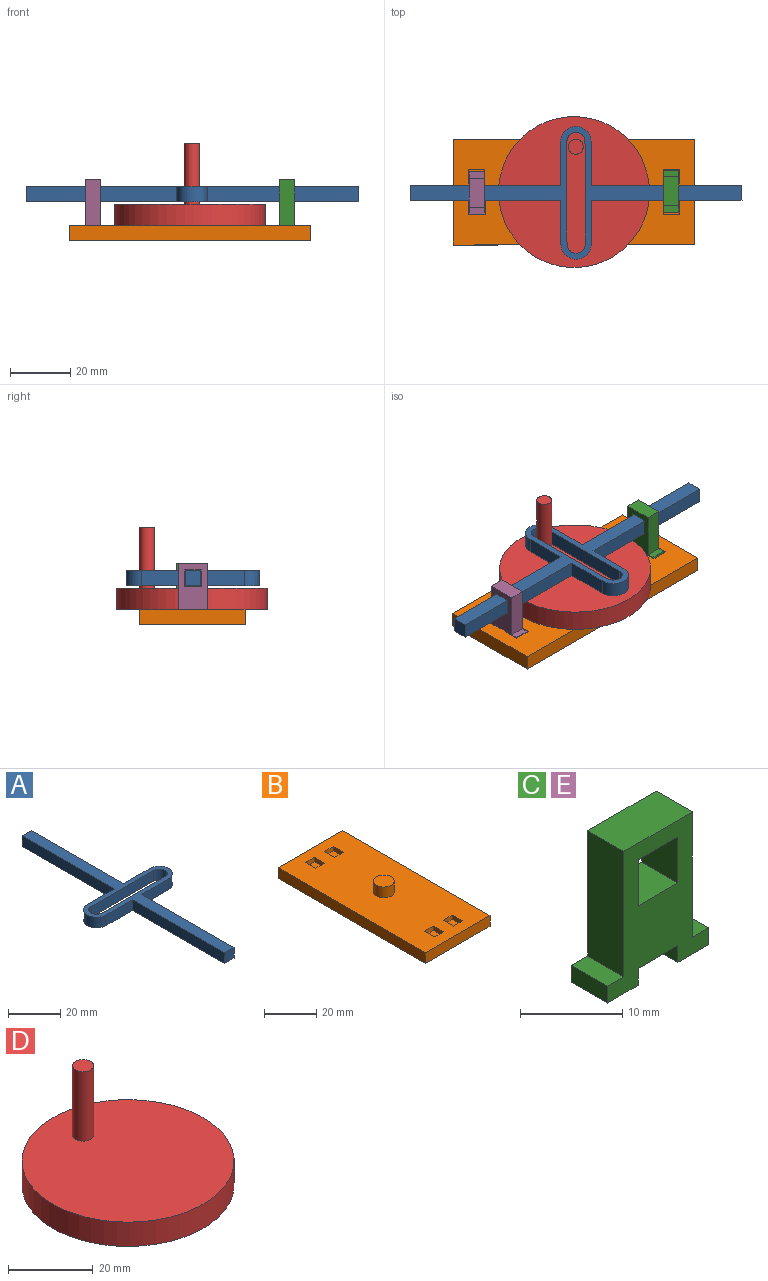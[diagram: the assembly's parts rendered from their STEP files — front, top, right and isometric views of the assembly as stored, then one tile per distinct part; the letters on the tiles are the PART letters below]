
ASSEMBLY  parts=5 mates=4
PART A: 18 faces, bbox 44x110x5 mm
  f0: extruded ~6x5mm, area 47.1mm2, adj f1,f15,f16,f17
  f1: plane 34x5mm, normal (0,-1,0), area 170mm2, adj f0,f2,f16,f17
  f2: cylinder r=3mm len=6mm, axis (0,0,-1), area 47.1mm2, adj f1,f15,f16,f17
  f3: plane 50x5mm, normal (-1,0,0), area 250mm2, adj f4,f14,f16,f17
  f4: plane 14.5x5mm, normal (0,1,0), area 72.5mm2, adj f3,f5,f16,f17
  f5: cylinder r=5mm len=10mm, axis (0,0,-1), area 78.5mm2, adj f4,f6,f16,f17
  f6: plane 14.5x5mm, normal (0,-1,0), area 72.5mm2, adj f5,f7,f16,f17
  f7: plane 50x5mm, normal (-1,0,0), area 250mm2, adj f6,f8,f16,f17
  f8: plane 5x5mm, normal (0,-1,0), area 25mm2, adj f7,f9,f16,f17
  f9: plane 50x5mm, normal (1,0,0), area 250mm2, adj f8,f10,f16,f17
  f10: plane 14.5x5mm, normal (0,-1,0), area 72.5mm2, adj f9,f11,f16,f17
  f11: cylinder r=5mm len=10mm, axis (0,0,-1), area 78.5mm2, adj f10,f12,f16,f17
  f12: plane 14.5x5mm, normal (0,1,0), area 72.5mm2, adj f11,f13,f16,f17
  f13: plane 50x5mm, normal (1,0,0), area 250mm2, adj f12,f14,f16,f17
  f14: plane 5x5mm, normal (0,1,0), area 25mm2, adj f3,f13,f16,f17
  f15: plane 34x5mm, normal (0,1,0), area 170mm2, adj f0,f2,f16,f17
  f16: plane 110x44mm, normal (0,0,1), area 686.3mm2, adj f0,f1,f2,f3,f4,f5,f6,f7
  f17: plane 110x44mm, normal (0,0,-1), area 686.3mm2, adj f0,f1,f2,f3,f4,f5,f6,f7
PART B: 28 faces, bbox 35x80x10 mm
  f0: plane 80x35mm, normal (0,0,1), area 2645.2mm2, adj f1,f2,f3,f4,f6,f7,f8,f9
  f1: plane 80x5mm, normal (1,0,0), area 400mm2, adj f0,f2,f4,f5
  f2: plane 35x5mm, normal (0,1,0), area 175mm2, adj f0,f1,f3,f5
  f3: plane 80x5mm, normal (-1,0,0), area 400mm2, adj f0,f2,f4,f5
  f4: plane 35x5mm, normal (0,-1,0), area 175mm2, adj f0,f1,f3,f5
  f5: plane 80x35mm, normal (0,0,-1), area 2800mm2, adj f1,f2,f3,f4
  f6: plane 5.5x2mm, normal (-1,0,0), area 11mm2, adj f0,f7,f9,f10
  f7: plane 4.75x2mm, normal (0,-1,0), area 9.5mm2, adj f0,f6,f8,f10
  f8: plane 5.5x2mm, normal (1,0,0), area 11mm2, adj f0,f7,f9,f10
  f9: plane 4.75x2mm, normal (0,1,0), area 9.5mm2, adj f0,f6,f8,f10
  f10: plane 5.5x4.75mm, normal (0,0,1), area 26.1mm2, adj f6,f7,f8,f9
  f11: plane 4.75x2mm, normal (0,-1,0), area 9.5mm2, adj f0,f12,f14,f15
  f12: plane 5.5x2mm, normal (1,0,0), area 11mm2, adj f0,f11,f13,f15
  f13: plane 4.75x2mm, normal (0,1,0), area 9.5mm2, adj f0,f12,f14,f15
  f14: plane 5.5x2mm, normal (-1,0,0), area 11mm2, adj f0,f11,f13,f15
  f15: plane 5.5x4.75mm, normal (0,0,1), area 26.1mm2, adj f11,f12,f13,f14
  f16: plane 4.75x2mm, normal (0,1,0), area 9.5mm2, adj f0,f17,f19,f20
  f17: plane 5.5x2mm, normal (-1,0,0), area 11mm2, adj f0,f16,f18,f20
  f18: plane 4.75x2mm, normal (0,-1,0), area 9.5mm2, adj f0,f17,f19,f20
  f19: plane 5.5x2mm, normal (1,0,0), area 11mm2, adj f0,f16,f18,f20
  f20: plane 5.5x4.75mm, normal (0,0,1), area 26.1mm2, adj f16,f17,f18,f19
  f21: plane 5.5x2mm, normal (-1,0,0), area 11mm2, adj f0,f22,f24,f25
  f22: plane 4.75x2mm, normal (0,-1,0), area 9.5mm2, adj f0,f21,f23,f25
  f23: plane 5.5x2mm, normal (1,0,0), area 11mm2, adj f0,f22,f24,f25
  f24: plane 4.75x2mm, normal (0,1,0), area 9.5mm2, adj f0,f21,f23,f25
  f25: plane 5.5x4.75mm, normal (0,0,1), area 26.1mm2, adj f21,f22,f23,f24
  f26: cylinder r=4mm len=8mm, axis (0,0,-1), area 125.7mm2, adj f0,f27
  f27: plane 8x8mm, normal (0,0,1), area 50.3mm2, adj f26
PART C: 18 faces, bbox 14x5x17 mm
  f0: plane 17x14mm, normal (0,1,0), area 129.2mm2, adj f2,f3,f4,f5,f6,f7,f8,f9
  f1: plane 17x14mm, normal (0,-1,0), area 129.3mm2, adj f2,f3,f4,f5,f6,f7,f8,f9
  f2: plane 5x2.25mm, normal (0,0,1), area 11.2mm2, adj f0,f1,f4,f16
  f3: plane 5x4.25mm, normal (0,0,-1), area 21.2mm2, adj f0,f1,f8,f16
  f4: plane 15x5mm, normal (-1,0,0), area 75mm2, adj f0,f1,f2,f13
  f5: plane 5x2.25mm, normal (0,0,1), area 11.2mm2, adj f0,f1,f7,f17
  f6: plane 5x4.25mm, normal (0,0,-1), area 21.2mm2, adj f0,f1,f10,f17
  f7: plane 15x5mm, normal (1,0,0), area 75mm2, adj f0,f1,f5,f13
  f8: plane 5x2mm, normal (1,0,0), area 10mm2, adj f0,f1,f3,f15
  f9: plane 5.5x5mm, normal (1,0,0), area 27.5mm2, adj f0,f1,f12,f14
  f10: plane 5x2mm, normal (-1,0,0), area 10mm2, adj f0,f1,f6,f15
  f11: plane 5.5x5mm, normal (-1,0,0), area 27.5mm2, adj f0,f1,f12,f14
  f12: plane 5.5x5mm, normal (0,0,-1), area 27.5mm2, adj f0,f1,f9,f11
  f13: plane 9.5x5mm, normal (0,0,1), area 47.5mm2, adj f0,f1,f4,f7
  f14: plane 5.5x5mm, normal (0,0,1), area 27.5mm2, adj f0,f1,f9,f11
  f15: plane 5.5x5mm, normal (0,0,-1), area 27.5mm2, adj f0,f1,f8,f10
  f16: plane 5x2mm, normal (-1,0,0), area 10mm2, adj f0,f1,f2,f3
  f17: plane 5x2mm, normal (1,0,0), area 10mm2, adj f0,f1,f5,f6
PART D: 7 faces, bbox 50x50x27 mm
  f0: cylinder r=25mm len=50mm, axis (0,0,-1), area 1099.6mm2, adj f1,f2
  f1: plane 50x50mm, normal (0,0,1), area 1943.9mm2, adj f0,f5
  f2: plane 50x50mm, normal (0,0,-1), area 1906.8mm2, adj f0,f3
  f3: cylinder r=4.25mm len=8.5mm, axis (0,0,-1), area 133.5mm2, adj f2,f4
  f4: plane 8.5x8.5mm, normal (0,0,-1), area 56.7mm2, adj f3
  f5: cylinder r=2.5mm len=20mm, axis (0,0,-1), area 314.2mm2, adj f1,f6
  f6: plane 5x5mm, normal (0,0,1), area 19.6mm2, adj f5
PART E: same geometry as C
PLACE A rot(axis=(0,0,-1),89.9deg) t=(68.54,-23.19,-8.65)mm
PLACE B rot(axis=(0,0,1),90.1deg) t=(67.89,-22.94,-21.4)mm
PLACE C rot(axis=(0,0,-1),89.9deg) t=(100.14,-22.65,-18.4)mm
PLACE D rot(axis=(0,0,-1),2.2deg) t=(67.89,-22.94,-16.4)mm
PLACE E rot(axis=(0,0,-1),89.9deg) t=(35.64,-23.23,-18.4)mm
MATE fastened E.f6 <-> B.f10  axis (0,0,-1) through (35.64,-28.1,-18.4)mm
MATE slider A.f8 <-> E.f1  axis (-1,0,0) through (13.54,-23.25,-6.15)mm
MATE fastened C.f3 <-> B.f15  axis (0,0,-1) through (100.13,-17.78,-18.4)mm
MATE revolute D.f3 <-> B.f26  axis (0,0,-1) through (67.89,-22.94,-11.4)mm
